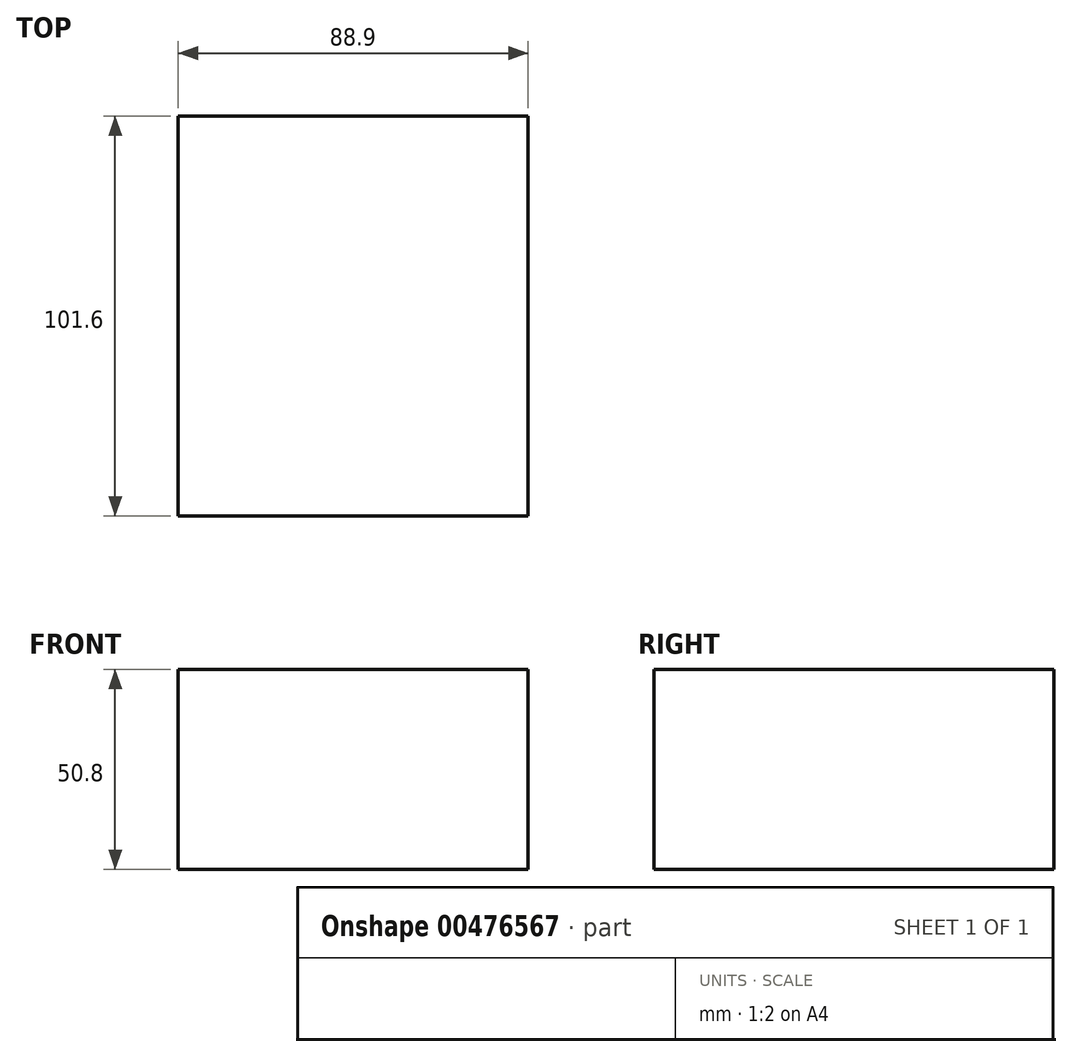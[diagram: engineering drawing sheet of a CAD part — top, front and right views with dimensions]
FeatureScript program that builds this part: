
annotation { "Feature Type Name" : "Feature", "Feature Type Description" : "" }
export const myFeature = defineFeature(function(context is Context, id is Id, definition is map)
    precondition{}
    {
        {
            var Q0;
            Q0=qCreatedBy(makeId("Front.planeOp"),FACE);
            var sketch = newSketch(context, id + "F0", { "sketchPlane" : qUnion([Q0])});
            skLineSegment(sketch, "E0", {"start": v(0, 0) * mm, "end": v(88.9, 0) * mm});
            skLineSegment(sketch, "E1", {"start": v(88.9, 0) * mm, "end": v(88.9, 50.8) * mm});
            skLineSegment(sketch, "E2", {"start": v(88.9, 50.8) * mm, "end": v(0, 50.8) * mm});
            skLineSegment(sketch, "E3", {"start": v(0, 50.8) * mm, "end": v(0, 0) * mm});
            skSolve(sketch);
        }
        {
            var Q0;
            Q0=makeQuery(id+"F0.imprint","IMPRINT",FACE,{"disambiguationData":[TD([[makeQuery(id+"F0.imprint","IMPRINT",EDGE,{"derivedFrom":sQuery(id+"F0.wireOp",EDGE,"E0")}),1.0]])]});
            extrude(context, id + "F1", {"entities" : qUnion([Q0]), "depth" : 101.6 * mm});
        }
    });
